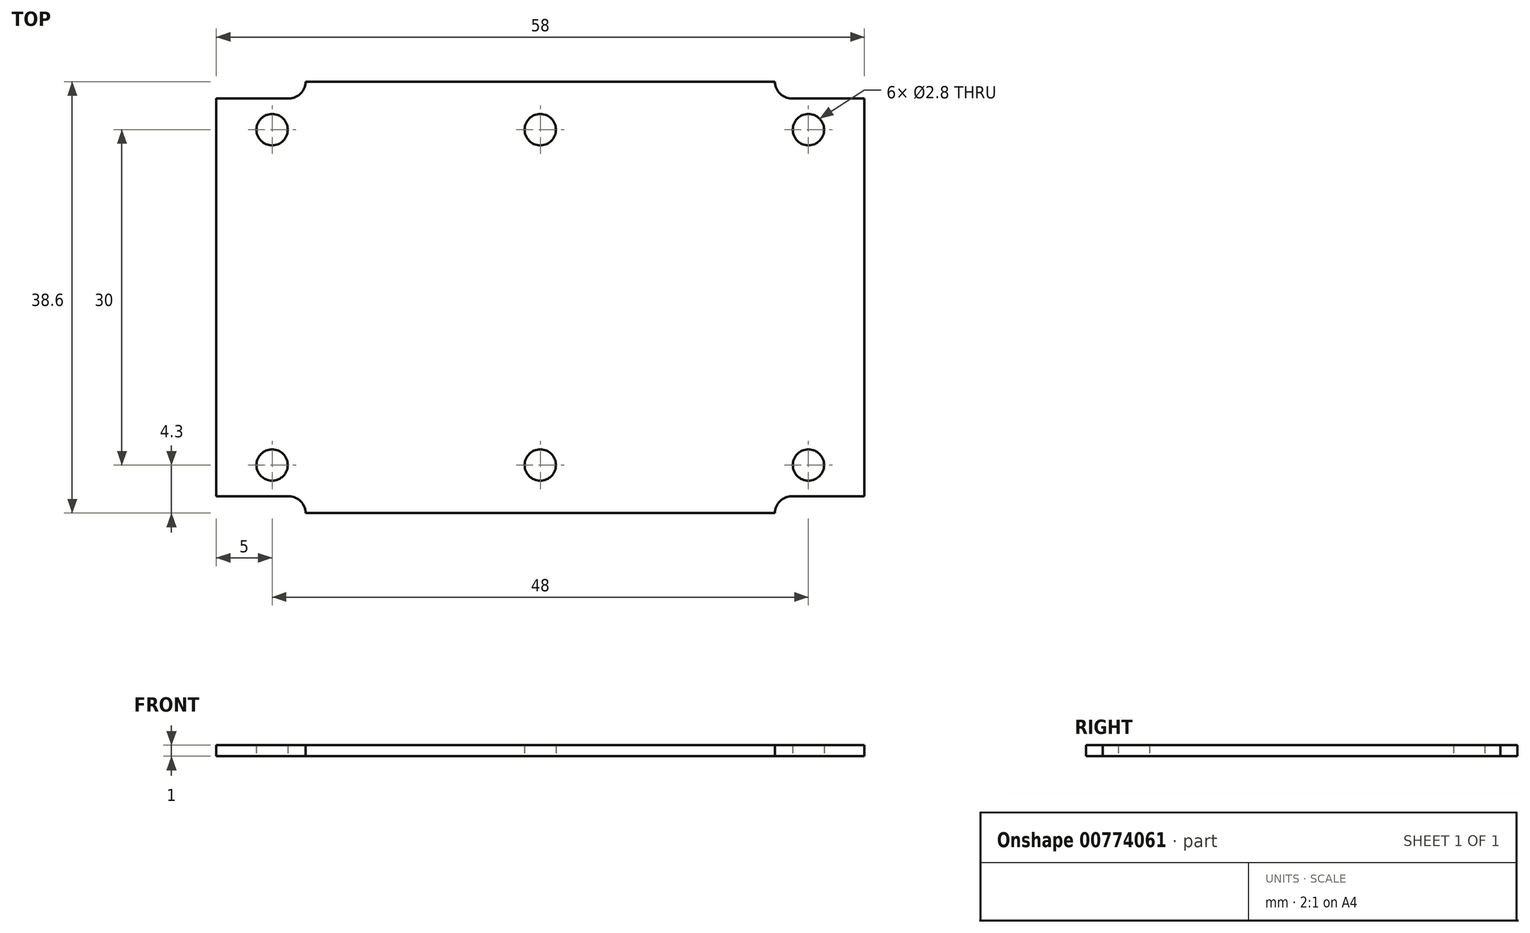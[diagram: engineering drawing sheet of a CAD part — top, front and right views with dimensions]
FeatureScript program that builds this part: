
annotation { "Feature Type Name" : "Feature", "Feature Type Description" : "" }
export const myFeature = defineFeature(function(context is Context, id is Id, definition is map)
    precondition{}
    {
        {
            var Q0;
            Q0=qCreatedBy(makeId("Top.planeOp"),FACE);
            var sketch = newSketch(context, id + "F0", { "sketchPlane" : qUnion([Q0])});
            skLineSegment(sketch, "E0", {"start": v(-29, 0) * mm, "end": v(29, 0) * mm, "construction": true});
            skLineSegment(sketch, "E1", {"start": v(0, 19.3) * mm, "end": v(0, -19.3) * mm, "construction": true});
            skLineSegment(sketch, "E2", {"start": v(22.5, 17.8) * mm, "end": v(29, 17.8) * mm});
            skArc(sketch, "E3", {"start": v(21, 19.3) * mm, "mid": v(21.44, 18.24) * mm, "end": v(22.5, 17.8) * mm});
            skLineSegment(sketch, "E4", {"start": v(29, 17.8) * mm, "end": v(29, 0) * mm});
            skLineSegment(sketch, "E5", {"start": v(21, 19.3) * mm, "end": v(0, 19.3) * mm});
            skCircle(sketch, "E6", {"center": v(24, 15) * mm, "radius": 1.4 * mm});
            skLineSegment(sketch, "E7.MirrorCS", {"start": v(-21, 19.3) * mm, "end": v(0, 19.3) * mm});
            skArc(sketch, "E8.MirrorCS", {"start": v(-21, 19.3) * mm, "mid": v(-21.44, 18.24) * mm, "end": v(-22.5, 17.8) * mm});
            skLineSegment(sketch, "E9.MirrorCS", {"start": v(-22.5, 17.8) * mm, "end": v(-29, 17.8) * mm});
            skLineSegment(sketch, "E10.MirrorCS", {"start": v(-29, 17.8) * mm, "end": v(-29, 0) * mm});
            skCircle(sketch, "E11.MirrorC", {"center": v(-24, 15) * mm, "radius": 1.4 * mm});
            skLineSegment(sketch, "E12.MirrorCS", {"start": v(-29, -17.8) * mm, "end": v(-29, 0) * mm});
            skLineSegment(sketch, "E13.MirrorCS", {"start": v(-22.5, -17.8) * mm, "end": v(-29, -17.8) * mm});
            skArc(sketch, "E14.MirrorCS", {"start": v(-21, -19.3) * mm, "mid": v(-21.44, -18.24) * mm, "end": v(-22.5, -17.8) * mm});
            skLineSegment(sketch, "E15.MirrorCS", {"start": v(-21, -19.3) * mm, "end": v(0, -19.3) * mm});
            skLineSegment(sketch, "E16.MirrorCS", {"start": v(21, -19.3) * mm, "end": v(0, -19.3) * mm});
            skArc(sketch, "E17.MirrorCS", {"start": v(21, -19.3) * mm, "mid": v(21.44, -18.24) * mm, "end": v(22.5, -17.8) * mm});
            skLineSegment(sketch, "E18.MirrorCS", {"start": v(22.5, -17.8) * mm, "end": v(29, -17.8) * mm});
            skLineSegment(sketch, "E19.MirrorCS", {"start": v(29, -17.8) * mm, "end": v(29, 0) * mm});
            skCircle(sketch, "E20.MirrorC", {"center": v(24, -15) * mm, "radius": 1.4 * mm});
            skCircle(sketch, "E21.MirrorC", {"center": v(-24, -15) * mm, "radius": 1.4 * mm});
            skCircle(sketch, "E22", {"center": v(0, -15) * mm, "radius": 1.4 * mm});
            skCircle(sketch, "E23", {"center": v(0, 15) * mm, "radius": 1.4 * mm});
            skSolve(sketch);
        }
        {
            var Q0;
            Q0 = qSketchRegion(id + "F0", true);
            extrude(context, id + "F1", {"entities" : qUnion([Q0]), "depth" : 1 * mm, "offsetDistance" : 25.4 * mm});
        }
    });
